# Revit family: Heater-Bromic-Tungsten-Gas-Portable
name_source: partatom
category: Mechanical Equipment
units: mm (PartAtom-declared; Revit-internal decimal feet)

## family parameters
Always vertical = No
Classification = None
Cut with Voids When Loaded = No
OmniClass Number = 23.75.10.17.14.14
OmniClass Title = Fuel-Fired Radiant Heaters
Part Type = Normal
Room Calculation Point = No
Round Connector Dimension = Use Diameter
Shared = No
Work Plane-Based = Yes

## types (2) — shared parameters
Approximate Heat Area = 215.00 SF
Depth = 27 "
Description = The award-winning Bromic Tungsten Smart-Heat™ Portable heater offers efficient heating in a stylish, modular, and maneuverable design with a neutral black finish.
Heater Material = Metal-Steel-Bromic-Black-Perforated
Height = 85 "
Manufacturer = Bromic Heating
Material = Metal-Steel-Bromic-Black
Model = Tungsten Smart-Heat™ Gas Portable
Mount Material = Metal-Steel-Bromic-Black
Product data url = https://www.bimobject.com
Screen Material = Metal-Steel-Bromic-Black
URL = https://www.bromic.com
Weight = 123.5 lbm
Width = 19 "
zero-valued in all types: Default Elevation

## per-type parameters (varying)
| type | LPG | Natural Gas | ProductCode |
| Tungsten Gas - NG - Portable | No | Yes | BH0510005 |
| Tungsten Gas - LPG - Portable | Yes | No | BH0510001 |

## geometry (parser evidence)
native form markers: Sweep x2
no freeform markers — native parametric forms only
